# Revit family: Shower-Shower_Column_Kit-KOHLER-Aleo-K-26246T-1
name_source: partatom
category: Plumbing Fixtures
units: mm (PartAtom-declared; Revit-internal decimal feet)

## family parameters
Cut with Voids When Loaded = No
Host = Face
Maintain Annotation Orientation = No
OmniClass Number = 23.31.17.00
Part Type = Normal
Room Calculation Point = No
Round Connector Dimension = Use Diameter
Shared = No

## types (6) — shared parameters
ADA Compliant = No
Assembly Code = D2010700
CW Connection = Yes
Cold Water Inlet = Cold Water Inlet
Date Modified = 01/10/2025
Default Elevation = 42"
Description = Double Shower Column – Rigid Pipe Connection (Rectangular Overhead)
Drain Included = No
Flow Rate = 3 GPM
HW Connection = Yes
Handle Clearance = 3 5/8"
Height = 51 15/16"
Hot Water Inlet = Hot Water Inlet
Length = 19 1/4"
Manufacturer = Kohler Co.
Master Format 2014 = 22 42 23
Master Format 2014 Name = Residential Showers
Material = Premium Metal Construction
Pressure = 80.00 psi
Product Documentation Link = https://files.kohler.com.cn
Product Name = Aleo
Product Page URL = https://www.kohler.com.cn
URL = http://www.kohler.com.cn
Vent Connection = No
Waste Connection = No
Waste Water Outlet = Waste Water Outlet
WaterSense Certified = No
Width = 5 7/8"

## per-type parameters (varying)
| type | B9_Handshower | B9_Showerhead | C9_Handshower | C9_Showerhead | Finish | Model | Secondary Finish | Type |
| 4, CP-Polished Chrome | Yes | No | No | Yes | Kohler-Metal-CP-Polished_Chrome | K-26246T-4-CP | Kohler-Plastic-0-White | 1 |
| 4, BL-Matte Black | Yes | No | No | Yes | Kohler-Metal-BL-Matte_Black | K-26246T-4-BL | Plastic-Pantone-PQ-194205-TCX | 2 |
| B4, BL-Matte Black | Yes | Yes | No | No | Kohler-Metal-BL-Matte_Black | K-26246T-B4-BL | Plastic-Pantone-PQ-194205-TCX | 3 |
| B4, CP-Polished Chrome | Yes | Yes | No | No | Kohler-Metal-CP-Polished_Chrome | K-26246T-B4-CP | Kohler-Plastic-0-White | 4 |
| C4, BL-Matte Black | No | No | Yes | Yes | Kohler-Metal-BL-Matte_Black | K-26246T-C4-BL | Plastic-Pantone-PQ-194205-TCX | 5 |
| C4, CP-Polished Chrome | No | No | Yes | Yes | Kohler-Metal-CP-Polished_Chrome | K-26246T-C4-CP | Kohler-Plastic-0-White | 6 |

## geometry (parser evidence)
native form markers: Sweep x6
no freeform markers — native parametric forms only
